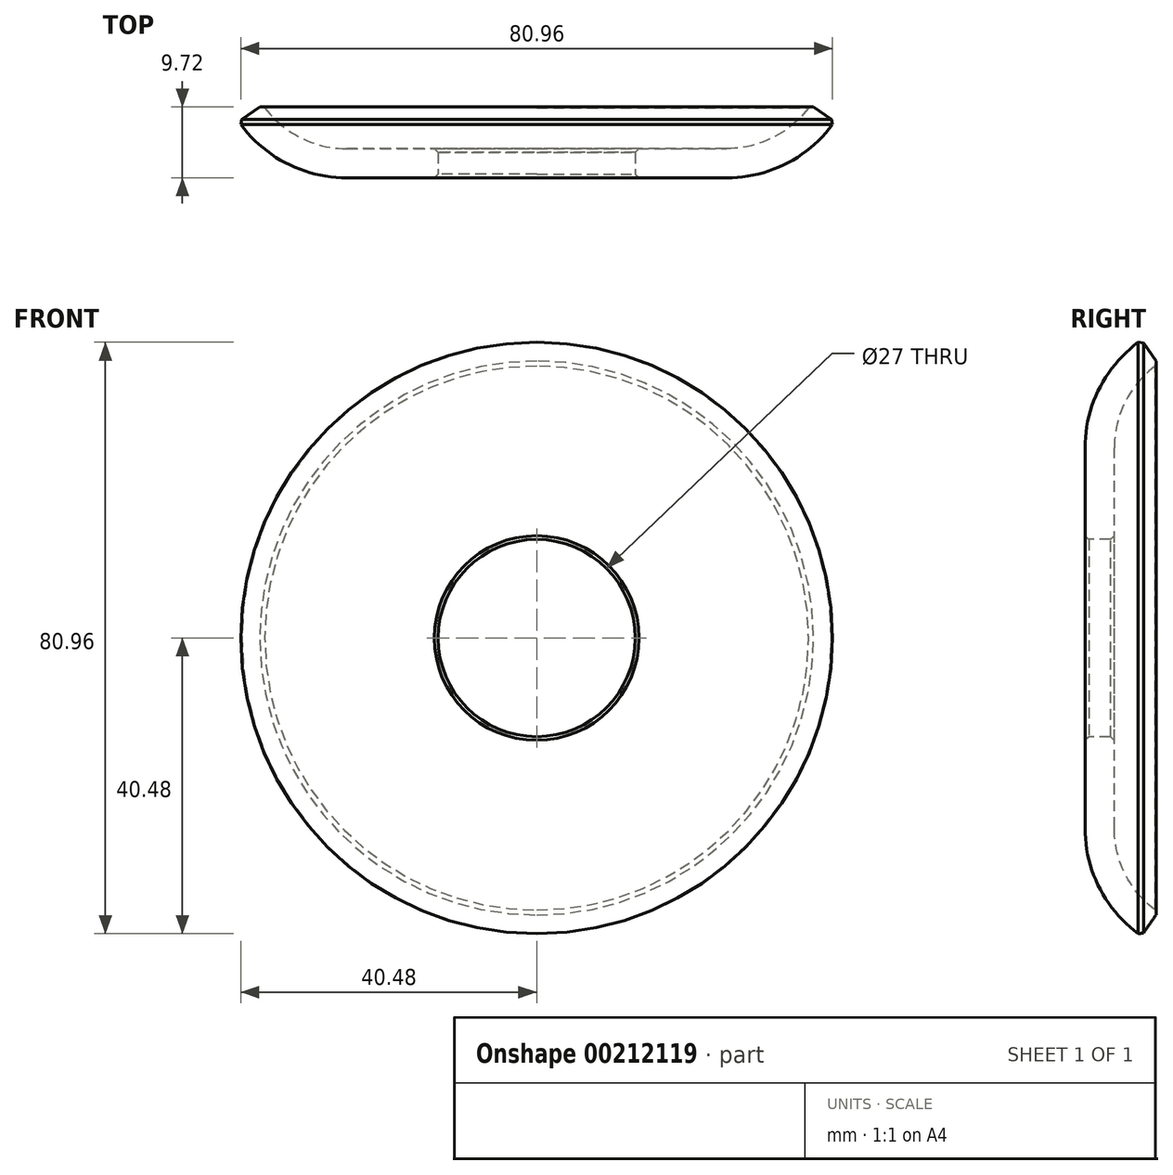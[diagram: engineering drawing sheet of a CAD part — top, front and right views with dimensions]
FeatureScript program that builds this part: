
annotation { "Feature Type Name" : "Feature", "Feature Type Description" : "" }
export const myFeature = defineFeature(function(context is Context, id is Id, definition is map)
    precondition{}
    {
        {
            var Q0;
            Q0=qCreatedBy(makeId("Top.planeOp"),FACE);
            var sketch = newSketch(context, id + "F0", { "sketchPlane" : qUnion([Q0])});
            skLineSegment(sketch, "E0", {"start": v(0, 0) * mm, "end": v(37.5, 0) * mm, "construction": true});
            skPoint(sketch, "E1", {"position": v(13.5, 0) * mm});
            skPoint(sketch, "E2", {"position": v(26, 0) * mm});
            skLineSegment(sketch, "E3.0", {"start": v(13.5, 4) * mm, "end": v(26, 4) * mm});
            skLineSegment(sketch, "E4", {"start": v(26, 0) * mm, "end": v(26, 6.23) * mm, "construction": true});
            skLineSegment(sketch, "E5", {"start": v(13.5, 0) * mm, "end": v(13.5, 4) * mm});
            skPoint(sketch, "E6", {"position": v(37.5, 10) * mm});
            skArc(sketch, "E7", {"start": v(26, 4) * mm, "mid": v(32.49, 5.6) * mm, "end": v(37.5, 10) * mm});
            skArc(sketch, "E8.0", {"start": v(26, 0) * mm, "mid": v(34.34, 2.04) * mm, "end": v(40.78, 7.71) * mm});
            skLineSegment(sketch, "E9", {"start": v(26, 0) * mm, "end": v(13.5, 0) * mm});
            skLineSegment(sketch, "E10", {"start": v(37.5, 10) * mm, "end": v(40.78, 7.71) * mm});
            skLineSegment(sketch, "E11", {"start": v(0, 0) * mm, "end": v(0, 10.7) * mm, "construction": true});
            skSolve(sketch);
        }
        {
            var Q0;
            Q0=makeQuery(id+"F0.imprint","IMPRINT",FACE,{"disambiguationData":[TD([[makeQuery(id+"F0.imprint","IMPRINT",EDGE,{"derivedFrom":sQuery(id+"F0.wireOp",EDGE,"E3.0")}),-1.0]])]});
            var Q1;
            Q1=sQuery(id+"F0.wireOp",EDGE,"E11");
            revolve(context, id + "F1", {"entities" : qUnion([Q0]), "axis" : qUnion([Q1]), "revolveType" : RevolveType.FULL});
        }
        {
            var Q0;
            Q0=makeQuery(id+"F1.opRevolve","SWEPT_FACE",FACE,{"disambiguationData":[OSD([sQuery(id+"F0.wireOp",EDGE,"E5")])]});
            var Q1;
            Q1=makeQuery(id+"F1.opRevolve","SWEPT_EDGE",EDGE,{"disambiguationData":[OSD([sQuery(id+"F0.wireOp",EDGE,"E7"),sQuery(id+"F0.wireOp",EDGE,"E10")])]});
            var Q2;
            Q2=makeQuery(id+"F1.opRevolve","SWEPT_EDGE",EDGE,{"disambiguationData":[OSD([sQuery(id+"F0.wireOp",EDGE,"E8.0"),sQuery(id+"F0.wireOp",EDGE,"E10")])]});
            chamfer(context, id + "F2", {"entities" : qUnion([Q0, Q1, Q2]), "width" : .5 * mm, "tangentPropagation" : true});
        }
    });
